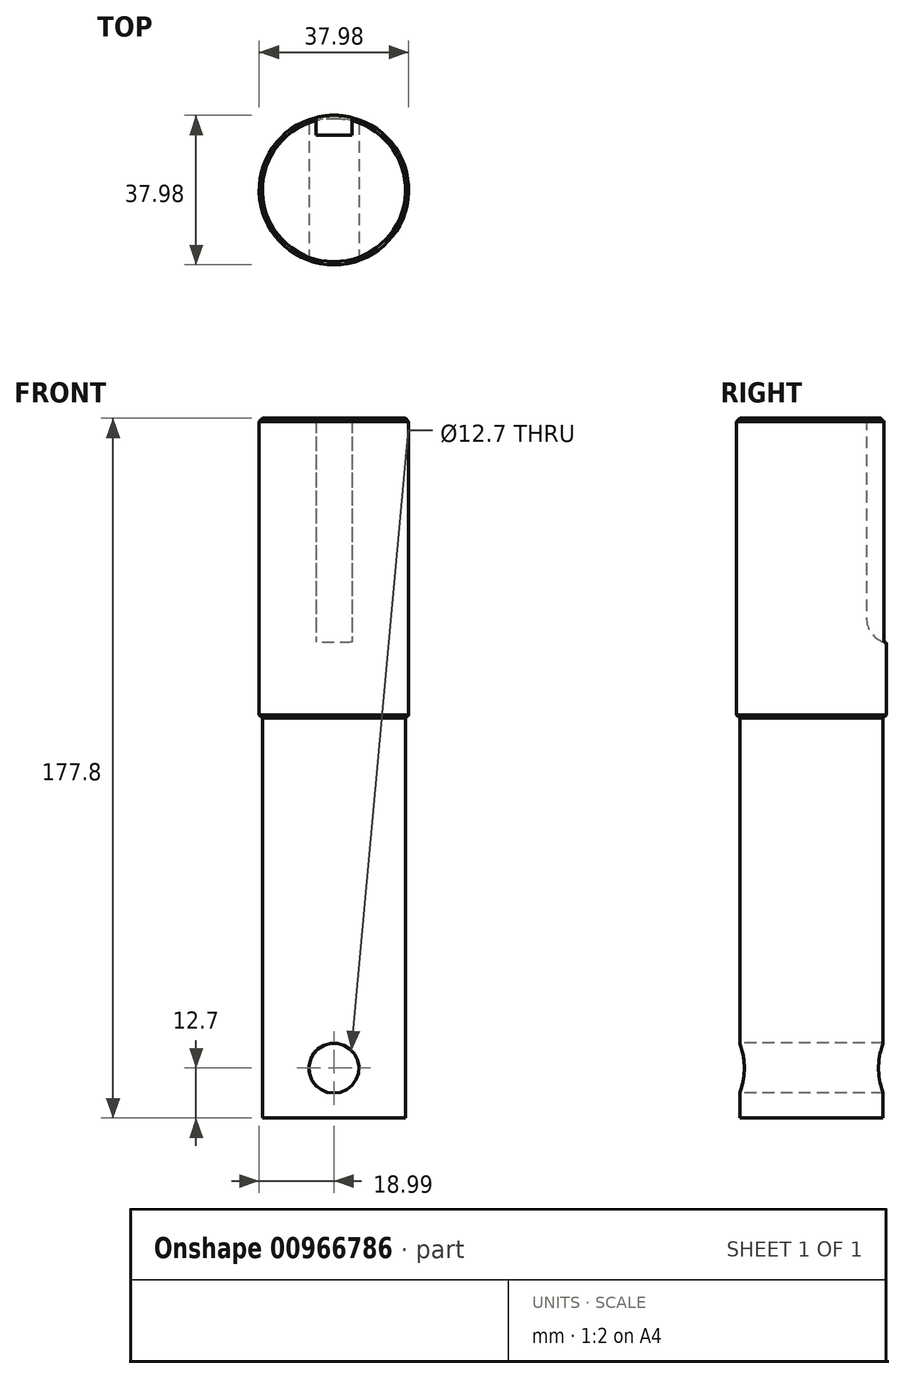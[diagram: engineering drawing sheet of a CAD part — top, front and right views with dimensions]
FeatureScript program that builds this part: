
annotation { "Feature Type Name" : "Feature", "Feature Type Description" : "" }
export const myFeature = defineFeature(function(context is Context, id is Id, definition is map)
    precondition{}
    {
        {
            var Q0;
            Q0=qCreatedBy(makeId("Top.planeOp"),FACE);
            var sketch = newSketch(context, id + "F0", { "sketchPlane" : qUnion([Q0])});
            skCircle(sketch, "E0", {"center": v(0, 0) * mm, "radius": 18.99 * mm});
            skSolve(sketch);
        }
        {
            var Q0;
            Q0=makeQuery(id+"F0.imprint","IMPRINT",FACE,{"disambiguationData":[TD([[makeQuery(id+"F0.imprint","IMPRINT",EDGE,{"derivedFrom":sQuery(id+"F0.wireOp",EDGE,"E0")}),1.0]])]});
            extrude(context, id + "F1", {"entities" : qUnion([Q0]), "endBound" : BoundingType.SYMMETRIC, "depth" : 76.2 * mm});
        }
        {
            var Q0;
            Q0=makeQuery(id+"F1.opExtrude","CAP_EDGE",EDGE,{"disambiguationData":[OSD([sQuery(id+"F0.wireOp",EDGE,"E0")])],"isStart":false});
            var Q1;
            Q1=makeQuery(id+"F1.opExtrude","CAP_EDGE",EDGE,{"disambiguationData":[OSD([sQuery(id+"F0.wireOp",EDGE,"E0")])],"isStart":true});
            chamfer(context, id + "F2", {"entities" : qUnion([Q0, Q1]), "width" : 0.8 * mm, "tangentPropagation" : true});
        }
        {
            var Q0;
            Q0=qCreatedBy(makeId("Right.planeOp"),FACE);
            var sketch = newSketch(context, id + "F3", { "sketchPlane" : qUnion([Q0])});
            skLineSegment(sketch, "E1", {"start": v(13.97, 38.1) * mm, "end": v(13.97, -12.7) * mm});
            skArc(sketch, "E2", {"start": v(13.97, -12.7) * mm, "mid": v(15.4, -16.72) * mm, "end": v(19.05, -18.92) * mm});
            skLineSegment(sketch, "E3", {"start": v(13.97, 38.1) * mm, "end": v(19.05, 38.1) * mm});
            skLineSegment(sketch, "E4", {"start": v(19.05, 38.1) * mm, "end": v(19.05, -18.92) * mm});
            skSolve(sketch);
        }
        {
            var Q0;
            Q0=qSketchRegion(id+"F3",true);
            extrude(context, id + "F4", {"entities" : qUnion([Q0]), "operationType" : NewBodyOperationType.REMOVE, "endBound" : BoundingType.SYMMETRIC, "depth" : 9.14 * mm});
        }
        {
            var Q0;
            Q0=makeQuery(id+"F1.opExtrude","CAP_FACE",FACE,{"disambiguationData":[OSD([sQuery(id+"F0.wireOp",EDGE,"E0")])],"isStart":true});
            var sketch = newSketch(context, id + "F5", { "sketchPlane" : qUnion([Q0])});
            skSolve(sketch);
        }
        {
            var Q0;
            {var subQ0=sQuery(id+"F0.wireOp",EDGE,"E0");Q0=makeQuery(id+"F5.imprint","IMPRINT",FACE,{"disambiguationData":[TD([[makeQuery(id+"F5.imprint","IMPRINT",EDGE,{"derivedFrom":makeQuery(id+"F2.opChamfer","BLEND_EDGE",EDGE,{"blendedFrom":[makeQuery(id+"F1.opExtrude","CAP_EDGE",EDGE,{"disambiguationData":[OSD([subQ0])],"isStart":true}),makeQuery(id+"F1.opExtrude","CAP_FACE",FACE,{"disambiguationData":[OSD([subQ0])],"isStart":true})],"blendedInto":[makeQuery(id+"F1.opExtrude","CAP_FACE",FACE,{"disambiguationData":[OSD([subQ0])],"isStart":true})]})}),1.0]])]});}
            extrude(context, id + "F6", {"entities" : qUnion([Q0]), "operationType" : NewBodyOperationType.ADD, "depth" : 101.6 * mm});
        }
        {
            var Q0;
            Q0=qCreatedBy(makeId("Front.planeOp"),FACE);
            var sketch = newSketch(context, id + "F7", { "sketchPlane" : qUnion([Q0])});
            skCircle(sketch, "E5", {"center": v(0, -127) * mm, "radius": 6.35 * mm});
            skSolve(sketch);
        }
        {
            var Q0;
            Q0=qSketchRegion(id+"F7",true);
            extrude(context, id + "F8", {"entities" : qUnion([Q0]), "operationType" : NewBodyOperationType.REMOVE, "endBound" : BoundingType.SYMMETRIC, "oppositeDirection" : true, "depth" : 76.2 * mm});
        }
    });
